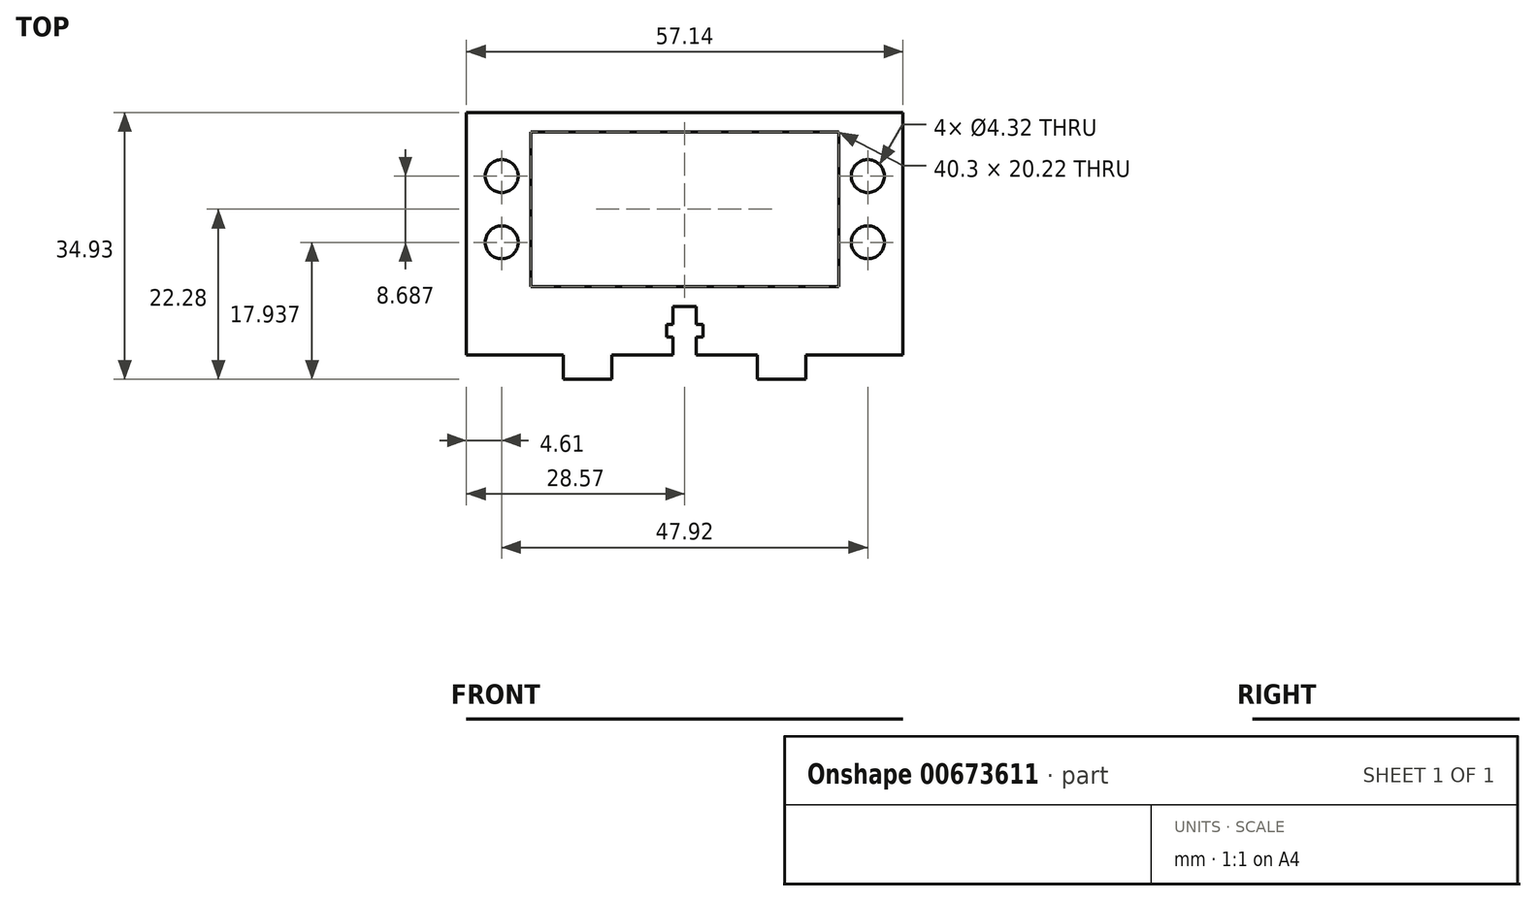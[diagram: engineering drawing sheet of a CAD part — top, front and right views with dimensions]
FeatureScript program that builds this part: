
annotation { "Feature Type Name" : "Feature", "Feature Type Description" : "" }
export const myFeature = defineFeature(function(context is Context, id is Id, definition is map)
    precondition{}
    {
        {
            var Q0;
            Q0=qCreatedBy(makeId("Top.planeOp"),FACE);
            var sketch = newSketch(context, id + "F0", { "sketchPlane" : qUnion([Q0])});
            skLineSegment(sketch, "E0.bottom", {"start": v(28.57, 12.65) * mm, "end": v(-28.58, 12.65) * mm});
            skLineSegment(sketch, "E0.top", {"start": v(28.57, -19.1) * mm, "end": v(15.88, -19.1) * mm});
            skLineSegment(sketch, "E0.left", {"start": v(28.58, 12.65) * mm, "end": v(28.58, -19.1) * mm});
            skLineSegment(sketch, "E0.right", {"start": v(-28.58, 12.65) * mm, "end": v(-28.58, -19.1) * mm});
            skPoint(sketch, "E0.middle", {"position": v(0, 0) * mm});
            skLineSegment(sketch, "E1.top", {"start": v(-9.53, -22.28) * mm, "end": v(-15.88, -22.28) * mm});
            skLineSegment(sketch, "E1.left", {"start": v(-9.52, -19.1) * mm, "end": v(-9.52, -22.28) * mm});
            skLineSegment(sketch, "E1.right", {"start": v(-15.88, -19.1) * mm, "end": v(-15.87, -22.28) * mm});
            skPoint(sketch, "E1.middle", {"position": v(-12.7, -19.1) * mm});
            skPoint(sketch, "E2.orphan", {"position": v(-9.53, -15.93) * mm});
            skPoint(sketch, "E3.orphan", {"position": v(-15.88, -15.93) * mm});
            skLineSegment(sketch, "E4.trimOffspring", {"start": v(-15.88, -19.1) * mm, "end": v(-28.58, -19.1) * mm});
            skLineSegment(sketch, "E5.MirrorCS", {"start": v(9.52, -19.1) * mm, "end": v(9.52, -22.28) * mm});
            skLineSegment(sketch, "E6.MirrorCS", {"start": v(9.53, -22.28) * mm, "end": v(15.88, -22.28) * mm});
            skLineSegment(sketch, "E7.MirrorCS", {"start": v(15.88, -19.1) * mm, "end": v(15.87, -22.28) * mm});
            skLineSegment(sketch, "E8.trimOffspring", {"start": v(9.53, -19.1) * mm, "end": v(1.52, -19.1) * mm});
            skLineSegment(sketch, "E9.bottom", {"start": v(20.15, 10.1) * mm, "end": v(-20.15, 10.1) * mm});
            skLineSegment(sketch, "E9.top", {"start": v(20.15, -10.1) * mm, "end": v(-20.15, -10.1) * mm});
            skLineSegment(sketch, "E9.left", {"start": v(20.15, 10.1) * mm, "end": v(20.15, -10.1) * mm});
            skLineSegment(sketch, "E9.right", {"start": v(-20.15, 10.1) * mm, "end": v(-20.15, -10.1) * mm});
            skLineSegment(sketch, "E10", {"start": v(0, 0) * mm, "end": v(23.96, 0) * mm, "construction": true});
            skPoint(sketch, "E10.endSnap0", {"position": v(20.15, 0) * mm});
            skLineSegment(sketch, "E11", {"start": v(23.96, 0) * mm, "end": v(23.96, 4.34) * mm, "construction": true});
            skCircle(sketch, "E12", {"center": v(23.96, 4.34) * mm, "radius": 2.16 * mm});
            skCircle(sketch, "E13.MirrorC", {"center": v(23.96, -4.34) * mm, "radius": 2.16 * mm});
            skCircle(sketch, "E14.MirrorC", {"center": v(-23.96, 4.34) * mm, "radius": 2.16 * mm});
            skCircle(sketch, "E15.MirrorC", {"center": v(-23.96, -4.34) * mm, "radius": 2.16 * mm});
            skLineSegment(sketch, "E16.top", {"start": v(1.52, -12.75) * mm, "end": v(-1.52, -12.75) * mm});
            skLineSegment(sketch, "E16.left", {"start": v(1.52, -19.1) * mm, "end": v(1.52, -16.76) * mm});
            skLineSegment(sketch, "E16.right", {"start": v(-1.52, -19.1) * mm, "end": v(-1.52, -16.76) * mm});
            skPoint(sketch, "E16.middle", {"position": v(0, -15.93) * mm});
            skLineSegment(sketch, "E17.bottom", {"start": v(2.38, -15.09) * mm, "end": v(1.52, -15.09) * mm});
            skLineSegment(sketch, "E17.top", {"start": v(2.38, -16.76) * mm, "end": v(1.52, -16.76) * mm});
            skLineSegment(sketch, "E17.left", {"start": v(2.38, -15.09) * mm, "end": v(2.38, -16.76) * mm});
            skLineSegment(sketch, "E17.right", {"start": v(-2.38, -15.09) * mm, "end": v(-2.38, -16.76) * mm});
            skLineSegment(sketch, "E18.trimOffspring", {"start": v(-1.52, -15.09) * mm, "end": v(-2.38, -15.09) * mm});
            skLineSegment(sketch, "E19.trimOffspring", {"start": v(-1.52, -15.09) * mm, "end": v(-1.52, -12.75) * mm});
            skLineSegment(sketch, "E20.trimOffspring", {"start": v(-1.52, -16.76) * mm, "end": v(-2.38, -16.76) * mm});
            skLineSegment(sketch, "E21.trimOffspring", {"start": v(1.52, -15.09) * mm, "end": v(1.52, -12.75) * mm});
            skLineSegment(sketch, "E22.trimOffspring", {"start": v(-1.52, -19.1) * mm, "end": v(-9.53, -19.1) * mm});
            skSolve(sketch);
        }
        {
            var Q0;
            Q0=makeQuery(id+"F0.imprint","IMPRINT",FACE,{"disambiguationData":[TD([[makeQuery(id+"F0.imprint","IMPRINT",EDGE,{"derivedFrom":sQuery(id+"F0.wireOp",EDGE,"E0.bottom")}),1.0]])]});
            extrude(context, id + "F1", {"entities" : qUnion([Q0]), "depth" : 1 / 203.2 * mm});
        }
    });
